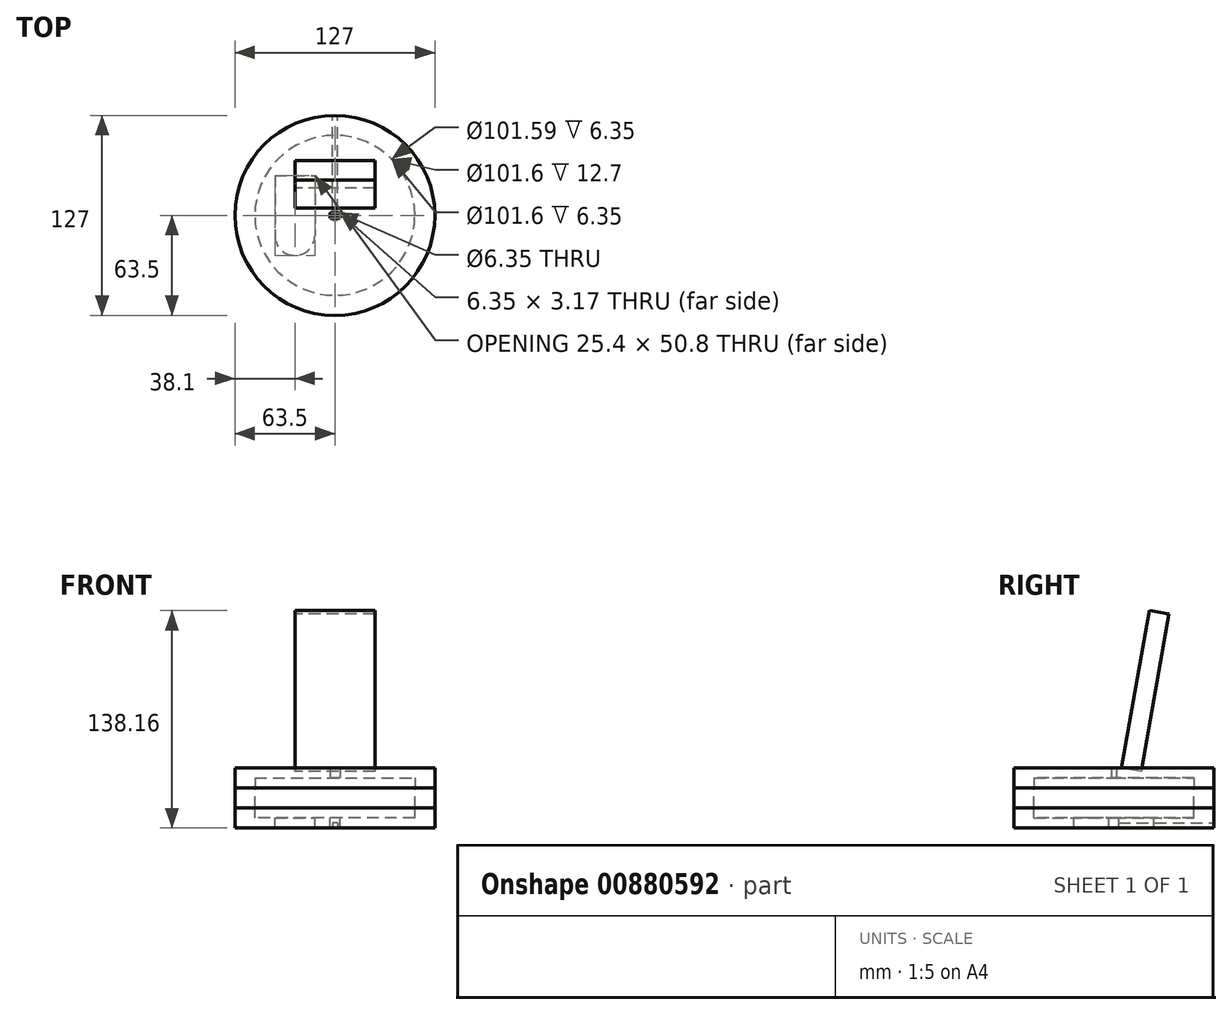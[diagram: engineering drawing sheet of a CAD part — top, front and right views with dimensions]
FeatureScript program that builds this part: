
annotation { "Feature Type Name" : "Feature", "Feature Type Description" : "" }
export const myFeature = defineFeature(function(context is Context, id is Id, definition is map)
    precondition{}
    {
        {
            var Q0;
            Q0=qCreatedBy(makeId("Top.planeOp"),FACE);
            var sketch = newSketch(context, id + "F0", { "sketchPlane" : qUnion([Q0])});
            skCircle(sketch, "E0", {"center": v(0, 0) * mm, "radius": 63.5 * mm});
            skSolve(sketch);
        }
        {
            var Q0;
            Q0=makeQuery(id+"F0.imprint","IMPRINT",FACE,{"disambiguationData":[TD([[makeQuery(id+"F0.imprint","IMPRINT",EDGE,{"derivedFrom":sQuery(id+"F0.wireOp",EDGE,"E0")}),1.0]])]});
            extrude(context, id + "F1", {"entities" : qUnion([Q0]), "depth" : 12.7 * mm, "offsetDistance" : 25.4 * mm});
        }
        {
            var Q0;
            Q0=makeQuery(id+"F1.opExtrude","CAP_FACE",FACE,{"disambiguationData":[OSD([sQuery(id+"F0.wireOp",EDGE,"E0")])],"isStart":false});
            extrude(context, id + "F2", {"entities" : qUnion([Q0]), "depth" : 12.7 * mm, "offsetDistance" : 25.4 * mm});
        }
        {
            var Q0;
            Q0=makeQuery(id+"F2.opExtrude","CAP_FACE",FACE,{"disambiguationData":[OSD([sQuery(id+"F0.wireOp",EDGE,"E0")])],"isStart":false});
            var sketch = newSketch(context, id + "F3", { "sketchPlane" : qUnion([Q0])});
            skCircle(sketch, "E1", {"center": v(0, 0) * mm, "radius": 50.8 * mm});
            skSolve(sketch);
        }
        {
            var Q0;
            Q0=makeQuery(id+"F3.imprint","IMPRINT",FACE,{"disambiguationData":[TD([[makeQuery(id+"F3.imprint","IMPRINT",EDGE,{"derivedFrom":sQuery(id+"F3.wireOp",EDGE,"E1")}),1.0]])]});
            extrude(context, id + "F4", {"entities" : qUnion([Q0]), "operationType" : NewBodyOperationType.REMOVE, "oppositeDirection" : true, "depth" : 12.7 * mm, "offsetDistance" : 25.4 * mm});
        }
        {
            var Q0;
            Q0=makeQuery(id+"F3.imprint","IMPRINT",FACE,{"disambiguationData":[TD([[makeQuery(id+"F3.imprint","IMPRINT",EDGE,{"derivedFrom":sQuery(id+"F3.wireOp",EDGE,"E1")}),1.0]])]});
            var Q1;
            Q1=makeQuery(id+"F3.imprint","IMPRINT",FACE,{"disambiguationData":[TD([[makeQuery(id+"F3.imprint","IMPRINT",EDGE,{"derivedFrom":sQuery(id+"F3.wireOp",EDGE,"E1")}),-1.0]])]});
            extrude(context, id + "F5", {"entities" : qUnion([Q0, Q1]), "depth" : 12.7 * mm, "offsetDistance" : 25.4 * mm});
        }
        {
            var Q0;
            Q0=makeQuery(id+"F1.opExtrude","CAP_FACE",FACE,{"disambiguationData":[OSD([sQuery(id+"F0.wireOp",EDGE,"E0")])],"isStart":false});
            var sketch = newSketch(context, id + "F6", { "sketchPlane" : qUnion([Q0])});
            skCircle(sketch, "E2", {"center": v(0, 0) * mm, "radius": 50.8 * mm});
            skSolve(sketch);
        }
        {
            var Q0;
            Q0=makeQuery(id+"F6.imprint","IMPRINT",FACE,{"disambiguationData":[TD([[makeQuery(id+"F6.imprint","IMPRINT",EDGE,{"derivedFrom":sQuery(id+"F6.wireOp",EDGE,"E2")}),1.0]])]});
            extrude(context, id + "F7", {"entities" : qUnion([Q0]), "operationType" : NewBodyOperationType.REMOVE, "oppositeDirection" : true, "depth" : 6.35 * mm, "offsetDistance" : 25.4 * mm});
        }
        {
            var Q0;
            Q0=makeQuery(id+"F7.boolean.opBoolean","COPY",FACE,{"derivedFrom":makeQuery(id+"F7.opExtrude","CAP_FACE",FACE,{"disambiguationData":[OSD([sQuery(id+"F6.wireOp",EDGE,"E2")])],"isStart":false})});
            var sketch = newSketch(context, id + "F8", { "sketchPlane" : qUnion([Q0])});
            skCircle(sketch, "E3", {"center": v(0, 0) * mm, "radius": 3.18 * mm});
            skSolve(sketch);
        }
        {
            var Q0;
            Q0=makeQuery(id+"F8.imprint","IMPRINT",FACE,{"disambiguationData":[TD([[makeQuery(id+"F8.imprint","IMPRINT",EDGE,{"derivedFrom":sQuery(id+"F8.wireOp",EDGE,"E3")}),1.0]])]});
            extrude(context, id + "F9", {"entities" : qUnion([Q0]), "operationType" : NewBodyOperationType.REMOVE, "oppositeDirection" : true, "depth" : 6.35 * mm, "offsetDistance" : 25.4 * mm});
        }
        {
            var Q0;
            Q0=makeQuery(id+"F7.boolean.opBoolean","COPY",FACE,{"derivedFrom":makeQuery(id+"F7.opExtrude","CAP_FACE",FACE,{"disambiguationData":[OSD([sQuery(id+"F6.wireOp",EDGE,"E2")])],"isStart":false})});
            var sketch = newSketch(context, id + "F10", { "sketchPlane" : qUnion([Q0])});
            skPoint(sketch, "E4", {"position": v(0, 0) * mm});
            skPoint(sketch, "E5", {"position": v(0, 25.4) * mm});
            skPoint(sketch, "E6", {"position": v(0, -25.4) * mm});
            skPoint(sketch, "E7", {"position": v(-25.4, 25.4) * mm});
            skPoint(sketch, "E8", {"position": v(-25.4, -25.4) * mm});
            skLineSegment(sketch, "E9", {"start": v(-25.4, 25.4) * mm, "end": v(-12.7, 25.4) * mm});
            skLineSegment(sketch, "E10", {"start": v(-12.7, 25.4) * mm, "end": v(-12.7, -12.7) * mm});
            skLineSegment(sketch, "E11", {"start": v(-25.4, 25.4) * mm, "end": v(-38.1, 25.4) * mm});
            skLineSegment(sketch, "E12", {"start": v(-38.1, 25.4) * mm, "end": v(-38.1, -12.7) * mm});
            skArc(sketch, "E13", {"start": v(-38.1, -12.7) * mm, "mid": v(-25.4, -25.4) * mm, "end": v(-12.7, -12.7) * mm});
            skSolve(sketch);
        }
        {
            var Q0;
            Q0=makeQuery(id+"F10.imprint","IMPRINT",FACE,{"disambiguationData":[TD([[makeQuery(id+"F10.imprint","IMPRINT",EDGE,{"derivedFrom":sQuery(id+"F10.wireOp",EDGE,"E9")}),-1.0]])]});
            extrude(context, id + "F11", {"entities" : qUnion([Q0]), "operationType" : NewBodyOperationType.REMOVE, "oppositeDirection" : true, "depth" : 6.35 * mm, "offsetDistance" : 25.4 * mm});
        }
        {
            var Q0;
            Q0=makeQuery(id+"F1.opExtrude","CAP_FACE",FACE,{"disambiguationData":[OSD([sQuery(id+"F0.wireOp",EDGE,"E0")])],"isStart":true});
            var sketch = newSketch(context, id + "F12", { "sketchPlane" : qUnion([Q0])});
            skPoint(sketch, "E14", {"position": v(-1.59, -2.75) * mm});
            skPoint(sketch, "E15", {"position": v(1.59, -2.75) * mm});
            skLineSegment(sketch, "E16", {"start": v(1.59, -2.75) * mm, "end": v(1.59, -63.48) * mm});
            skLineSegment(sketch, "E17", {"start": v(-1.59, -2.75) * mm, "end": v(-1.59, -63.48) * mm});
            skSolve(sketch);
        }
        {
            var Q0;
            {var subQ0=sQuery(id+"F12.wireOp",EDGE,"E16");Q0=makeQuery(id+"F12.imprint","IMPRINT",FACE,{"disambiguationData":[TD([[makeQuery(id+"F12.imprint","IMPRINT",EDGE,{"derivedFrom":subQ0}),-1.0]])]});}
            extrude(context, id + "F13", {"entities" : qUnion([Q0]), "operationType" : NewBodyOperationType.REMOVE, "oppositeDirection" : true, "depth" : 3.17 * mm, "offsetDistance" : 25.4 * mm});
        }
        {
            var Q0;
            Q0=makeQuery(id+"F5.opExtrude","CAP_FACE",FACE,{"disambiguationData":[OSD([sQuery(id+"F0.wireOp",EDGE,"E0")])],"isStart":true});
            var sketch = newSketch(context, id + "F14", { "sketchPlane" : qUnion([Q0])});
            skCircle(sketch, "E18", {"center": v(0, 0) * mm, "radius": 50.8 * mm});
            skSolve(sketch);
        }
        {
            var Q0;
            Q0=makeQuery(id+"F14.imprint","IMPRINT",FACE,{"disambiguationData":[TD([[makeQuery(id+"F14.imprint","IMPRINT",EDGE,{"derivedFrom":sQuery(id+"F14.wireOp",EDGE,"E18")}),1.0]])]});
            extrude(context, id + "F15", {"entities" : qUnion([Q0]), "operationType" : NewBodyOperationType.REMOVE, "oppositeDirection" : true, "depth" : 6.35 * mm, "offsetDistance" : 25.4 * mm});
        }
        {
            var Q0;
            Q0=makeQuery(id+"F15.boolean.opBoolean","COPY",FACE,{"derivedFrom":makeQuery(id+"F15.opExtrude","CAP_FACE",FACE,{"disambiguationData":[OSD([sQuery(id+"F14.wireOp",EDGE,"E18")])],"isStart":false})});
            var sketch = newSketch(context, id + "F16", { "sketchPlane" : qUnion([Q0])});
            skLineSegment(sketch, "E19.bottom", {"start": v(3.17, 1.59) * mm, "end": v(-3.18, 1.59) * mm});
            skLineSegment(sketch, "E19.top", {"start": v(3.18, -1.59) * mm, "end": v(-3.17, -1.59) * mm});
            skLineSegment(sketch, "E19.left", {"start": v(3.17, 1.59) * mm, "end": v(3.18, -1.59) * mm});
            skLineSegment(sketch, "E19.right", {"start": v(-3.18, 1.59) * mm, "end": v(-3.17, -1.59) * mm});
            skPoint(sketch, "E19.middle", {"position": v(0, 0) * mm});
            skSolve(sketch);
        }
        {
            var Q0;
            Q0=makeQuery(id+"F16.imprint","IMPRINT",FACE,{"disambiguationData":[TD([[makeQuery(id+"F16.imprint","IMPRINT",EDGE,{"derivedFrom":sQuery(id+"F16.wireOp",EDGE,"E19.bottom")}),1.0]])]});
            extrude(context, id + "F17", {"entities" : qUnion([Q0]), "operationType" : NewBodyOperationType.REMOVE, "oppositeDirection" : true, "depth" : 6.35 * mm, "offsetDistance" : 25.4 * mm});
        }
        {
            var Q0;
            Q0=qCreatedBy(makeId("Right.planeOp"),FACE);
            var sketch = newSketch(context, id + "F18", { "sketchPlane" : qUnion([Q0])});
            skPoint(sketch, "E20", {"position": v(0, 38.1) * mm});
            skPoint(sketch, "E21", {"position": v(1.59, 38.1) * mm});
            skPoint(sketch, "E22", {"position": v(4.76, 38.1) * mm});
            skLineSegment(sketch, "E23", {"start": v(4.76, 38.1) * mm, "end": v(4.76, 38.1) * mm});
            skLineSegment(sketch, "E24", {"start": v(4.76, 38.1) * mm, "end": v(4.76, 139.7) * mm});
            skLineSegment(sketch, "E25", {"start": v(4.76, 139.7) * mm, "end": v(17.46, 139.7) * mm});
            skLineSegment(sketch, "E26", {"start": v(17.46, 139.7) * mm, "end": v(17.46, 38.1) * mm});
            skLineSegment(sketch, "E27", {"start": v(17.46, 38.1) * mm, "end": v(4.76, 38.1) * mm});
            skSolve(sketch);
        }
        {
            var Q0;
            Q0=makeQuery(id+"F18.imprint","IMPRINT",FACE,{"disambiguationData":[TD([[makeQuery(id+"F18.imprint","IMPRINT",EDGE,{"derivedFrom":sQuery(id+"F18.wireOp",EDGE,"E24")}),-1.0]])]});
            extrude(context, id + "F19", {"entities" : qUnion([Q0]), "depth" : 25.4 * mm, "offsetDistance" : 25.4 * mm});
        }
        {
            var Q0;
            Q0=makeQuery(id+"F18.imprint","IMPRINT",FACE,{"disambiguationData":[TD([[makeQuery(id+"F18.imprint","IMPRINT",EDGE,{"derivedFrom":sQuery(id+"F18.wireOp",EDGE,"E24")}),-1.0]])]});
            extrude(context, id + "F20", {"entities" : qUnion([Q0]), "oppositeDirection" : true, "depth" : 25.4 * mm, "offsetDistance" : 25.4 * mm});
        }
        {
            var Q0;
            Q0=makeQuery(id+"F19.opExtrude","SWEPT_BODY",BODY,{"disambiguationData":[OSD([sQuery(id+"F18.wireOp",EDGE,"E24"),sQuery(id+"F18.wireOp",EDGE,"E25"),sQuery(id+"F18.wireOp",EDGE,"E26"),sQuery(id+"F18.wireOp",EDGE,"E27")])]});
            var Q1;
            Q1=makeQuery(id+"F20.opExtrude","SWEPT_BODY",BODY,{"disambiguationData":[OSD([sQuery(id+"F18.wireOp",EDGE,"E24"),sQuery(id+"F18.wireOp",EDGE,"E25"),sQuery(id+"F18.wireOp",EDGE,"E26"),sQuery(id+"F18.wireOp",EDGE,"E27")])]});
            booleanBodies(context, id + "F21", {"operationType" : BooleanOperationType.UNION, "tools" : qUnion([Q0, Q1])});
        }
        {
            var Q0;
            Q0=makeQuery(id+"F19.opExtrude","SWEPT_BODY",BODY,{"disambiguationData":[OSD([sQuery(id+"F18.wireOp",EDGE,"E24"),sQuery(id+"F18.wireOp",EDGE,"E25"),sQuery(id+"F18.wireOp",EDGE,"E26"),sQuery(id+"F18.wireOp",EDGE,"E27")])]});
            var Q1;
            {var subQ0=sQuery(id+"F18.wireOp",EDGE,"E27");var subQ1=sQuery(id+"F18.wireOp",EDGE,"E24");Q1=makeQuery(id+"F21.opBoolean","MERGE",EDGE,{"derivedFrom":[makeQuery(id+"F19.opExtrude","SWEPT_EDGE",EDGE,{"disambiguationData":[OSD([subQ1,subQ0])]}),makeQuery(id+"F20.opExtrude","SWEPT_EDGE",EDGE,{"disambiguationData":[OSD([subQ1,subQ0])]})]});}
            var Q2;
            {var subQ0=sQuery(id+"F18.wireOp",EDGE,"E27");var subQ1=sQuery(id+"F18.wireOp",EDGE,"E24");Q2=makeQuery(id+"F21.opBoolean","MERGE",EDGE,{"derivedFrom":[makeQuery(id+"F19.opExtrude","SWEPT_EDGE",EDGE,{"disambiguationData":[OSD([subQ1,subQ0])]}),makeQuery(id+"F20.opExtrude","SWEPT_EDGE",EDGE,{"disambiguationData":[OSD([subQ1,subQ0])]})]});}
            transform(context, id + "F22", {"entities" : qUnion([Q0]), "transformType" : TransformType.ROTATION, "transformAxis" : qUnion([Q2]), "angle" : 10 * degree, "makeCopy" : false});
        }
    });
